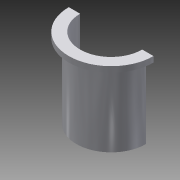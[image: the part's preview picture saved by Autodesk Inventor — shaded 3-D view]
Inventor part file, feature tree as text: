
AUTODESK INVENTOR PART (.ipt)
format: ipt  version: 2015 (Build 190159000, 159)  size: 122,368 bytes
history: native  units: in
note: dims shown in document units (in); Inventor stores cm internally (conversion verified against a paired STEP export)
features: revolve x1, sketch x1
ambient origin geometry x8: Origin, YZ Plane, XZ Plane, XY Plane, X Axis, Y Axis, Z Axis, Center Point
bodies: Solid1 (feature_tree)
feature tree (2):
  revolve  "Revolution1"  [1 undecoded]
  sketch  "Sketch1"  dims[d0=0.75in d1=1.0in d2=0.2185in d3=2.594in d4=0.5841in d5=0.5in d6=1.844in d7=0.5in d8=1.75in d9=0.25in d10=105.0deg d11=0.5in d12=0.5in d13=0.25in d14=0.375in d15=2.0in d16=0.5in d17=0.25in d18=0.234in d19=0.25in d20=2.0in d21=0.25in d22=105.0deg d23=0.125in d24=0.25in d25=2.3995in d26=0.125in d27=0.25in d28=180.0deg]
note: 1 required parameter value undecoded (feature->parameter linkage not recoverable at this tier; creation-order binding heuristic only, values carry confidence <= 0.55)
